# Revit family: QF_Icetro_IM-1100-RC_RH
name_source: partatom
category: Specialty Equipment
units: mm (PartAtom-declared; Revit-internal decimal feet)

## family parameters
Always vertical = Yes
Cut with Voids When Loaded = No
OmniClass Number = 23.40.40.00
OmniClass Title = Food Service Equipment and Furnishings
Part Type = Normal
Room Calculation Point = No
Round Connector Dimension = Use Diameter
Shared = No
Work Plane-Based = Yes

## types (4) — shared parameters
Assembly Code = E1090300
BTUH = 17647.0 Btu/h
Chilled Water Flow = 0 GPM
Chilled Water Maximum Pressure = 80.00 psi
Chilled Water Minimum Pressure = 20.00 psi
Chilled Water Return Size = 0"
Chilled Water Supply Size = 0"
Chilled Water Temperature = -460 °F
Conn Plug = NEMA 5-15P
Cycle = 60 Hz
Default Elevation = 48 "
Depth = 24.8 "
Description = Ice Cube Machine
FL Amps = 16 A
Foodservice Equipment Identifier = Yes
Height = 30.3 "
Indirect Waste Flow = 0 GPM
Indirect Waste Size = 1"
Manufacturer = Icetro
Max Overcurrent Protection = 25 A
Min Ckt Ampacity = 16 A
Phase = 1
URL = https://www.icetroamerica.com
URL Cutsheet = https://www.icetroamerica.com
Watts = 4720 W
Weight in Pounds = 231.5
Width = 30 "
zero-valued in all types: Chilled Water Return Connection Height, Chilled Water Return RI Height, Chilled Water Supply Connection Height, Chilled Water Supply RI Height, Elec Conn Connection Height, Indirect Waste Connection Height

## per-type parameters (varying)
| type | Apparent Power | Model | Volts |
| 208/60/1 IM-1100-RC | 3245 VA | IM-1100-RC | 208 V |
| 208/60/1 IM-1100-RH | 3245 VA | IM-1100-RH | 208 V |
| 230/60/1 IM-1100-RC | 3588 VA | IM-1100-RC | 230 V |
| 230/60/1 IM-1100-RH | 3588 VA | IM-1100-RH | 230 V |

## geometry (parser evidence)
native form markers: Sweep x5
no freeform markers — native parametric forms only
